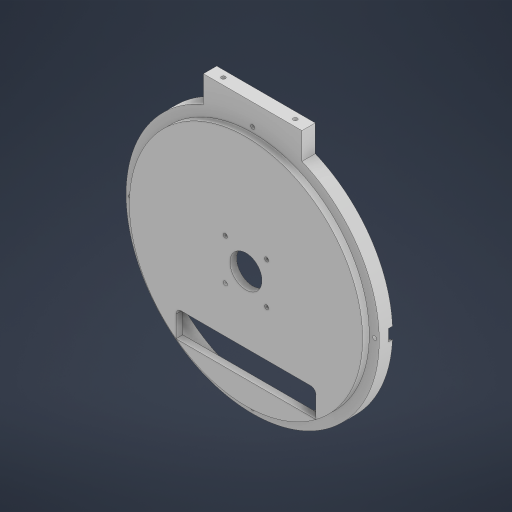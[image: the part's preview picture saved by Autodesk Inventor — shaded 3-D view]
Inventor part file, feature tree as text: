
AUTODESK INVENTOR PART (.ipt)
format: ipt  version: 2023 (Build 270158000, 158)  size: 328,192 bytes
history: native  units: mm
features: extrude x11, sketch x7, fillet x2
ambient origin geometry x8: Origin, YZ Plane, XZ Plane, XY Plane, X Axis, Y Axis, Z Axis, Center Point
bodies: Solid1 (feature_tree)
feature tree (20):
  extrude  "Extrusion1"  Depth=10.0mm TaperAngle=0.0deg
  extrude  "Extrusion2"  Depth=10.0mm TaperAngle=0.0deg
  extrude  "Extrusion3"  Depth=5.0mm
  sketch  "Sketch3"  dims[d0=190.0mm d2=10.0mm d3=0.0mm]
  extrude  "Extrusion8"  Depth=23.5mm
  sketch  "Sketch8"  dims[d14=47.0mm d15=23.5mm]
  extrude  "Extrusion10"  Depth=3.0mm
  extrude  "Extrusion11"  Depth=3.0mm
  extrude  "Extrusion7"  Depth=2.0mm TaperAngle=0.0deg
  extrude  "Extrusion9"  Depth=3.0mm
  extrude  "Extrusion12"  Depth=2.0mm
  extrude  "Extrusion13"  Depth=10.0mm TaperAngle=0.0deg
  fillet  "Fillet2"  Radius=11.0mm
  extrude  "Extrusion14"  Depth=2.0mm
  fillet  "Fillet3"  Radius=11.0mm
  sketch  "Sketch6"  dims[d4=175.0mm d5=10.0mm d6=0.0mm]
  sketch  "Sketch7"  dims[d7=5.0mm d8=0.0mm d13=47.0mm]
  sketch  "Sketch9"  dims[d16=23.5mm d26=3.0mm]
  sketch  "Sketch10"  dims[d27=3.0mm d28=3.0mm]
  sketch  "Sketch11"  dims[d29=3.0mm d30=70.0mm d31=0.0mm d34=3.0mm d35=24.0mm d36=10.0mm d37=0.0mm d38=11.0mm d39=11.0mm d40=11.0mm d41=11.0mm d42=3.0mm d43=0.0mm d44=180.0deg d45=20.0mm d46=10.0mm d47=0.0mm d48=10.0mm d49=0.0mm d50=10.0mm d51=10.0mm d52=3.0mm d53=3.0mm d54=10.0mm d55=0.0mm d56=50.0mm d57=20.0mm d58=20.0mm d59=20.0mm d60=10.0mm d61=0.0mm d62=4.0mm d63=10.0mm d64=10.0mm d65=10.0mm d66=10.0mm d67=3.0mm d68=0.0mm d69=2.0mm]
